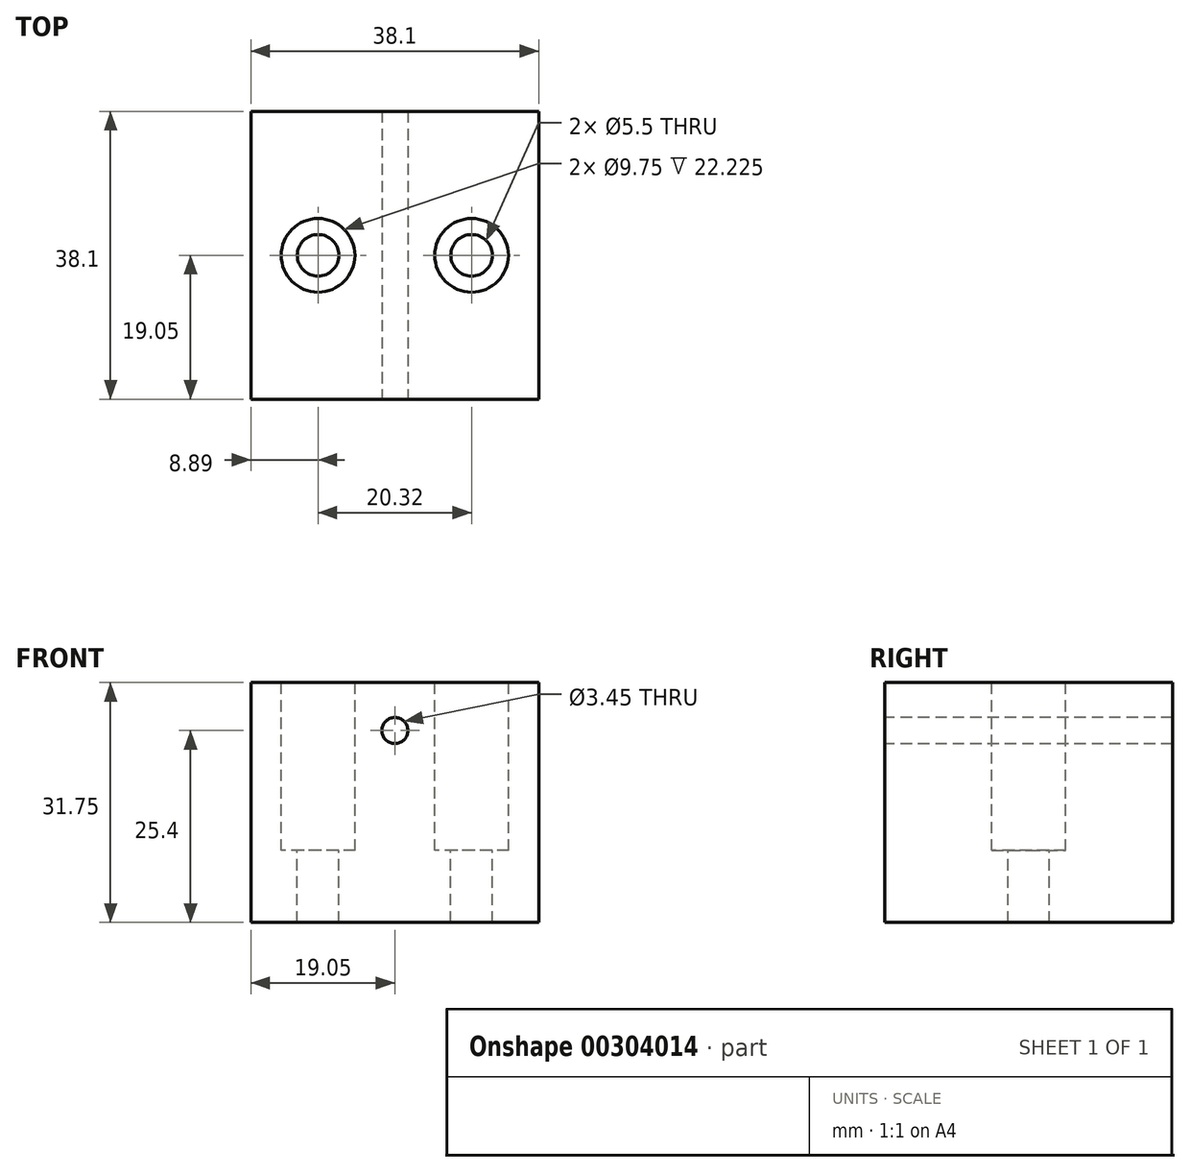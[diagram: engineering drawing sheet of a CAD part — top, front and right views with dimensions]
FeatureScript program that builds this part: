
annotation { "Feature Type Name" : "Feature", "Feature Type Description" : "" }
export const myFeature = defineFeature(function(context is Context, id is Id, definition is map)
    precondition{}
    {
        {
            var Q0;
            Q0=qCreatedBy(makeId("Top.planeOp"),FACE);
            var sketch = newSketch(context, id + "F0", { "sketchPlane" : qUnion([Q0])});
            skLineSegment(sketch, "E0.bottom", {"start": v(-19.05, 19.05) * mm, "end": v(19.05, 19.05) * mm});
            skLineSegment(sketch, "E0.top", {"start": v(-19.05, -19.05) * mm, "end": v(19.05, -19.05) * mm});
            skLineSegment(sketch, "E0.left", {"start": v(-19.05, 19.05) * mm, "end": v(-19.05, -19.05) * mm});
            skLineSegment(sketch, "E0.right", {"start": v(19.05, 19.05) * mm, "end": v(19.05, -19.05) * mm});
            skLineSegment(sketch, "E1", {"start": v(0, 19.05) * mm, "end": v(0, 0) * mm, "construction": true});
            skLineSegment(sketch, "E2", {"start": v(0, 0) * mm, "end": v(-19.05, 0) * mm, "construction": true});
            skSolve(sketch);
        }
        {
            var Q0;
            Q0 = qSketchRegion(id + "F0", true);
            extrude(context, id + "F1", {"entities" : qUnion([Q0]), "depth" : 31.75 * mm});
        }
        {
            var Q0;
            Q0=makeQuery(id+"F1.opExtrude","SWEPT_FACE",FACE,{"disambiguationData":[OSD([sQuery(id+"F0.wireOp",EDGE,"E0.top")])]});
            var sketch = newSketch(context, id + "F2", { "sketchPlane" : qUnion([Q0])});
            skLineSegment(sketch, "E3", {"start": v(0, 0) * mm, "end": v(0, 25.4) * mm});
            skPoint(sketch, "E3.endSnap0", {"position": v(0, 0) * mm});
            skSolve(sketch);
        }
        {
            var Q0;
            Q0=sQuery(id+"F2.wireOp",VERTEX,"E3.end");
            var Q1;
            Q1=makeQuery(id+"F1.opExtrude","SWEPT_BODY",BODY,{"disambiguationData":[OSD([sQuery(id+"F0.wireOp",EDGE,"E0.bottom"),sQuery(id+"F0.wireOp",EDGE,"E0.top"),sQuery(id+"F0.wireOp",EDGE,"E0.left"),sQuery(id+"F0.wireOp",EDGE,"E0.right")])]});
            hole(context, id + "F3", {"style" : HoleStyle.SIMPLE, "endStyle" : HoleEndStyle.THROUGH, "standardTappedOrClearance" : lookupTablePath({ "standard" : "ANSI", "engagement" : "75%", "pitch" : "32 tpi", "size" : "#8", "type" : "Tapped" }), "standardBlindInLast" : lookupTablePath({ "standard" : "ANSI", "engagement" : "75%", "pitch" : "32 tpi", "size" : "#8", "type" : "Tapped" }), "holeDiameter" : 3.45 * mm, "showTappedDepth" : true, "tappedDepth" : 12.7 * mm, "tapClearance" : 3, "startFromSketch" : true, "locations" : qUnion([Q0]), "scope" : qUnion([Q1]), "majorDiameter" : 4.17 * mm});
        }
        {
            var Q0;
            Q0=makeQuery(id+"F1.opExtrude","CAP_FACE",FACE,{"disambiguationData":[OSD([sQuery(id+"F0.wireOp",EDGE,"E0.bottom"),sQuery(id+"F0.wireOp",EDGE,"E0.top"),sQuery(id+"F0.wireOp",EDGE,"E0.left"),sQuery(id+"F0.wireOp",EDGE,"E0.right")])],"isStart":false});
            var sketch = newSketch(context, id + "F4", { "sketchPlane" : qUnion([Q0])});
            skLineSegment(sketch, "E4.bottom", {"start": v(-10.16, -10.16) * mm, "end": v(10.16, -10.16) * mm});
            skLineSegment(sketch, "E4.top", {"start": v(-10.16, 10.16) * mm, "end": v(10.16, 10.16) * mm});
            skLineSegment(sketch, "E4.left", {"start": v(-10.16, -10.16) * mm, "end": v(-10.16, 10.16) * mm});
            skLineSegment(sketch, "E4.right", {"start": v(10.16, -10.16) * mm, "end": v(10.16, 10.16) * mm});
            skPoint(sketch, "E4.middle", {"position": v(0, 0) * mm});
            skLineSegment(sketch, "E5", {"start": v(-10.16, 0) * mm, "end": v(10.16, 0) * mm});
            skLineSegment(sketch, "E6", {"start": v(0, 10.16) * mm, "end": v(0, -10.16) * mm});
            skSolve(sketch);
        }
        {
            var Q0;
            Q0=sQuery(id+"F4.wireOp",VERTEX,"E5.end");
            var Q1;
            Q1=sQuery(id+"F4.wireOp",VERTEX,"E5.start");
            var Q2;
            Q2=makeQuery(id+"F1.opExtrude","SWEPT_BODY",BODY,{"disambiguationData":[OSD([sQuery(id+"F0.wireOp",EDGE,"E0.bottom"),sQuery(id+"F0.wireOp",EDGE,"E0.top"),sQuery(id+"F0.wireOp",EDGE,"E0.left"),sQuery(id+"F0.wireOp",EDGE,"E0.right")])]});
            hole(context, id + "F5", {"style" : HoleStyle.C_BORE, "endStyle" : HoleEndStyle.THROUGH, "holeDiameter" : 5.5 * mm, "cBoreDiameter" : 9.75 * mm, "cBoreDepth" : 22.22 * mm, "tappedDepth" : 12.7 * mm, "tapClearance" : 3, "startFromSketch" : true, "locations" : qUnion([Q0, Q1]), "scope" : qUnion([Q2])});
        }
    });
